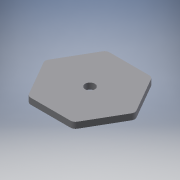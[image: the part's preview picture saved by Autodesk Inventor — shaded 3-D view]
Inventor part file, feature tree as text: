
AUTODESK INVENTOR PART (.ipt)
format: ipt  version: 2017 (Build 210142000, 142)  size: 128,000 bytes
history: native  units: mm
features: extrude x1, fillet x1, sketch x1
ambient origin geometry x8: Origin, YZ Plane, XZ Plane, XY Plane, X Axis, Y Axis, Z Axis, Center Point
bodies: Solid1 (feature_tree)
feature tree (3):
  extrude  "Extrusion1"  Depth=4.0mm
  fillet  "Fillet1"  Radius=2.7mm
  sketch  "Sketch1"  dims[d0=22.0mm d1=50.229473mm d2=2.7mm d3=65.0mm d4=8.0mm d5=5.0mm d6=0.0mm d7=4.0mm d8=80.0mm]
